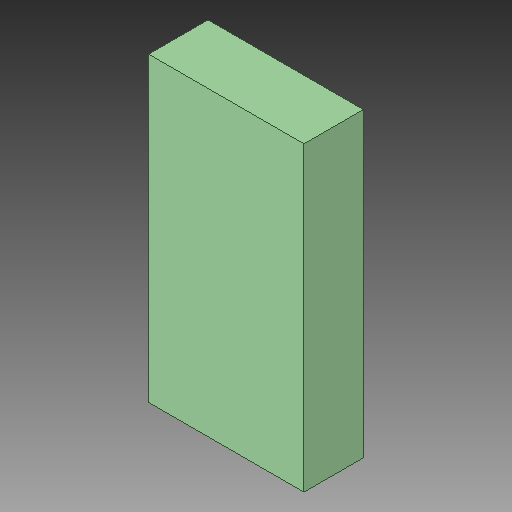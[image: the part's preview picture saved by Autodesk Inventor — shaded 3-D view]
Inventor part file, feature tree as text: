
AUTODESK INVENTOR PART (.ipt)
format: ipt  version: 2018 (Build 220112000, 112)  size: 79,872 bytes
history: native  units: in
note: dims shown in document units (in); Inventor stores cm internally (conversion verified against a paired STEP export)
features: other x1, extrude x1
ambient origin geometry x8: Origin, YZ Plane, XZ Plane, XY Plane, X Axis, Y Axis, Z Axis, Center Point
bodies: Solid1 (feature_tree)
feature tree (2):
  other  "JP1M, _3V3_61"
  extrude  "Extrusion1"  Depth=0.0394in TaperAngle=0.0deg
